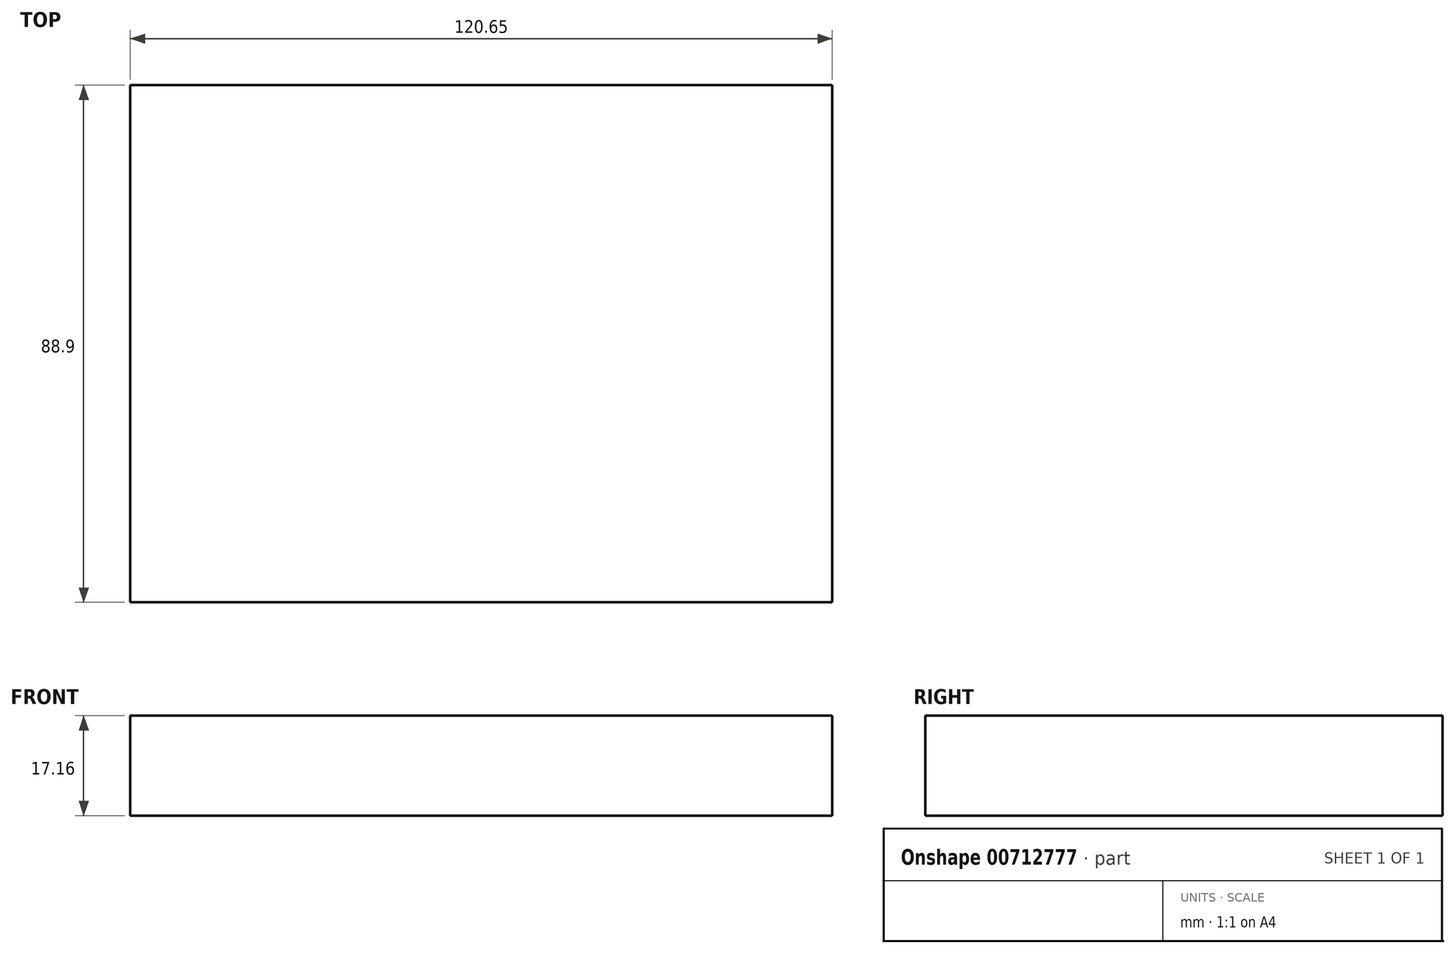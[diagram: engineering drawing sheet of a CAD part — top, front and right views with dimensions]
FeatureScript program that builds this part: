
annotation { "Feature Type Name" : "Feature", "Feature Type Description" : "" }
export const myFeature = defineFeature(function(context is Context, id is Id, definition is map)
    precondition{}
    {
        {
            var Q0;
            Q0=qCreatedBy(makeId("Front.planeOp"),FACE);
            var sketch = newSketch(context, id + "F0", { "sketchPlane" : qUnion([Q0])});
            skLineSegment(sketch, "E0.bottom", {"start": v(0, 0) * mm, "end": v(-120.65, 0) * mm});
            skLineSegment(sketch, "E0.top", {"start": v(0, 17.16) * mm, "end": v(-120.65, 17.16) * mm});
            skLineSegment(sketch, "E0.left", {"start": v(0, 0) * mm, "end": v(0, 17.16) * mm});
            skLineSegment(sketch, "E0.right", {"start": v(-120.65, 0) * mm, "end": v(-120.65, 17.16) * mm});
            skSolve(sketch);
        }
        {
            var Q0;
            Q0 = qSketchRegion(id + "F0", true);
            extrude(context, id + "F1", {"entities" : qUnion([Q0]), "depth" : 88.9 * mm, "offsetDistance" : 25.4 * mm});
        }
    });
